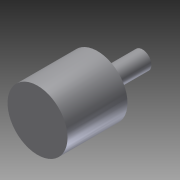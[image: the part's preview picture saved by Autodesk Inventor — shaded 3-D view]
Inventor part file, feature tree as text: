
AUTODESK INVENTOR PART (.ipt)
format: ipt  version: 2012 (Build 160160000, 160)  size: 80,384 bytes
history: native  units: mm
features: revolve x1, sketch x1
ambient origin geometry x8: Origin, YZ Plane, XZ Plane, XY Plane, X Axis, Y Axis, Z Axis, Center Point
bodies: Solid1 (feature_tree)
feature tree (2):
  revolve  "Revolution1"  [1 undecoded]
  sketch  "Sketch1"  dims[d0=10.0mm d1=3.0mm d2=15.0mm d3=20.0mm d4=90.0deg]
note: 1 required parameter value undecoded (feature->parameter linkage not recoverable at this tier; creation-order binding heuristic only, values carry confidence <= 0.55)
